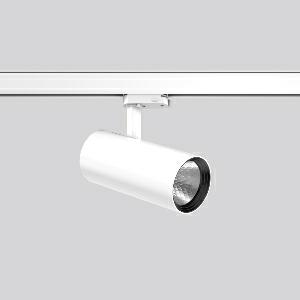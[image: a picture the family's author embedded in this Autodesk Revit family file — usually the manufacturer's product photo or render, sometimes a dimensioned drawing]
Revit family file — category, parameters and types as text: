
# Revit family: deecos_s_mini_742197_002_c384
name_source: partatom
category: Lighting Fixtures
units: mm (PartAtom-declared; Revit-internal decimal feet)

## family parameters
Cut with Voids When Loaded = No
Host = Face
Light Source = No
Part Type = Normal
Room Calculation Point = No
Round Connector Dimension = Use Diameter
Shared = No

## types (1)
- DEECOS S mini (1 x LED Modul 930, 2550 lm, 3000)
    Apparent Load = 20 VA
    Approval mark = CE
    CIE Flux Codes = 95 99 100 100 100
    Color Rendering = 90
    Color Temperature = 3000
    Default Elevation = 1800 mm
    Description = Series: DEECOS S mini
LED surface-mounted projector in modern design with no visible cooling ribs. Housing: die-cast aluminium, powder-coated. Rotation range: 356°. Swivel range: 90°. Black plastic ring and recessed LED to prevent glare from the side. Optical assembly with reflector made of MIRO-Silver with 98% total light reflection for outstanding efficiency - can be changed without tools. Best colour rendering index Ra>90. With multi adaptor for 3-circuit tracks 230 V. Suitable for Track on ceiling, Wall track. High quality converter without flickering and stroboscopic effect. The following accessories can be mounted without use of tools: interchangeable lenses, decorative glasses, honeycomb louvre, clear and frosted diffusers, white interchangeable plastic ring. 
Colour: traffic white, matt (RAL 9016)
Diameter: 87 mm
Height: 214 mm
Lamp: LED
Socket: without socket
Colour temperature: 3000K
Colour rendering index (CRI): 92
System power: 20 W
Rated luminous flux: 2550 lm
Beam angle Down: 60°
Luminous efficiency: 128 lm/W
Control gear: Regulated power supply
Protection class: I
Type of protection: IP 20
    Height = 214 mm
    Lamp = 1 x LED Modul 930
    Lamp Light Flux = 2550 lm
    Lamp count = 1
    Length = 87 mm
    Lifetime = 50000 h
    Luminous efficacy = 128 lm/W
    Manufacturer = RZB
    ModVariant = No
    Model = 742197.002
    Mounting Place = Ceiling
    Mounting Type = Rail mounted
    Number of Poles = 1
    OnlyDefault = Yes
    Power Factor = 1
    Product Name = DEECOS S mini
    Product group = Track mounted projectors
    ProductGroupID = 301
    Protection Class = Protection class I
    Protection Degree = IP 20
    RLX_Detail_Level = 1
    RLX_Emergency_Light_Flux = 0 lm
    RLX_Emergency_Type = 0
    RLX_Emergency_Type_DB = No
    RlxData = <blob elided: 35677 chars, md5=0ba81f5e>
    Socket = socket
    Standby Power = 0 W
    System Light Flux = 2550 lm
    System Power = 20 W
    Type Comments = ALEA SPOT
    Type Image = 741926.002.jpg
    URL = http://relux.com
    VarID = ---
    Voltage = 230 V
    Voltage Range = 220-240 V
    Weight = 0.00 kg
    Width = 0 mm  [stored 0 ft]

note: [stored X ft] marks values corroborated as IEEE doubles in the binary element streams (Revit-internal decimal feet)

## geometry (parser evidence)
native form markers: Blend x4, Sweep x12
no freeform markers — native parametric forms only
